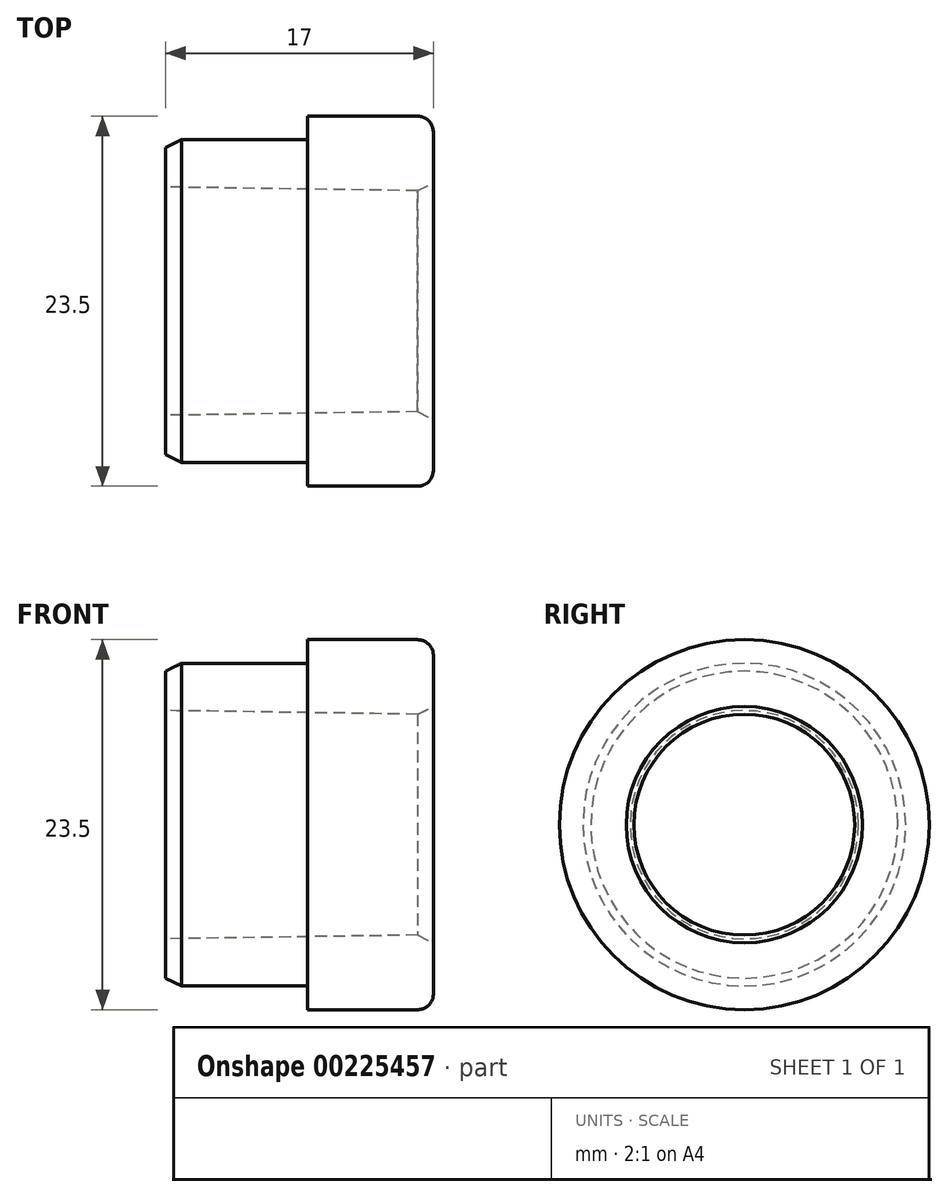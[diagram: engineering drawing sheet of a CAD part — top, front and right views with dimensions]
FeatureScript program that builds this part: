
annotation { "Feature Type Name" : "Feature", "Feature Type Description" : "" }
export const myFeature = defineFeature(function(context is Context, id is Id, definition is map)
    precondition{}
    {
        {
            var Q0;
            Q0=qCreatedBy(makeId("Top.planeOp"),FACE);
            var sketch = newSketch(context, id + "F0", { "sketchPlane" : qUnion([Q0])});
            skLineSegment(sketch, "E0", {"start": v(-17, 0) * mm, "end": v(0, 0) * mm, "construction": true});
            skLineSegment(sketch, "E1", {"start": v(0, 7) * mm, "end": v(0, 11.75) * mm});
            skLineSegment(sketch, "E2", {"start": v(0, 11.75) * mm, "end": v(-8, 11.75) * mm});
            skLineSegment(sketch, "E3", {"start": v(-8, 11.75) * mm, "end": v(-8, 10.25) * mm});
            skLineSegment(sketch, "E4", {"start": v(-8, 10.25) * mm, "end": v(-17, 10.25) * mm});
            skLineSegment(sketch, "E5", {"start": v(0, 7) * mm, "end": v(-17, 7.25) * mm});
            skLineSegment(sketch, "E6", {"start": v(-17, 7.25) * mm, "end": v(-17, 10.25) * mm});
            skLineSegment(sketch, "E7.MirrorCS", {"start": v(-17, -7.25) * mm, "end": v(-17, -10.25) * mm});
            skLineSegment(sketch, "E8.MirrorCS", {"start": v(0, -7) * mm, "end": v(0, -11.75) * mm});
            skLineSegment(sketch, "E9.MirrorCS", {"start": v(0, -11.75) * mm, "end": v(-8, -11.75) * mm});
            skLineSegment(sketch, "E10.MirrorCS", {"start": v(-8, -11.75) * mm, "end": v(-8, -10.25) * mm});
            skLineSegment(sketch, "E11.MirrorCS", {"start": v(-8, -10.25) * mm, "end": v(-17, -10.25) * mm});
            skLineSegment(sketch, "E12.MirrorCS", {"start": v(0, -7) * mm, "end": v(-17, -7.25) * mm});
            skSolve(sketch);
        }
        {
            var Q0;
            Q0=makeQuery(id+"F0.imprint","IMPRINT",FACE,{"disambiguationData":[TD([[makeQuery(id+"F0.imprint","IMPRINT",EDGE,{"derivedFrom":sQuery(id+"F0.wireOp",EDGE,"E7.MirrorCS")}),1.0]])]});
            var Q1;
            Q1=sQuery(id+"F0.wireOp",EDGE,"E0");
            revolve(context, id + "F1", {"entities" : qUnion([Q0]), "axis" : qUnion([Q1]), "revolveType" : RevolveType.FULL});
        }
        {
            var Q0;
            Q0=makeQuery(id+"F1.opRevolve","SWEPT_EDGE",EDGE,{"disambiguationData":[OSD([sQuery(id+"F0.wireOp",EDGE,"E7.MirrorCS"),sQuery(id+"F0.wireOp",EDGE,"E11.MirrorCS")])]});
            chamfer(context, id + "F2", {"entities" : qUnion([Q0]), "chamferType" : ChamferType.TWO_OFFSETS, "width1" : 0.5 * mm, "oppositeDirection" : false, "width2" : 1 * mm, "tangentPropagation" : true});
        }
        {
            var Q0;
            Q0=makeQuery(id+"F1.opRevolve","SWEPT_EDGE",EDGE,{"disambiguationData":[OSD([sQuery(id+"F0.wireOp",EDGE,"E8.MirrorCS"),sQuery(id+"F0.wireOp",EDGE,"E12.MirrorCS")])]});
            chamfer(context, id + "F3", {"entities" : qUnion([Q0]), "chamferType" : ChamferType.TWO_OFFSETS, "width1" : 1 * mm, "oppositeDirection" : true, "width2" : 0.5 * mm, "tangentPropagation" : true});
        }
        {
            var Q0;
            Q0=makeQuery(id+"F1.opRevolve","SWEPT_EDGE",EDGE,{"disambiguationData":[OSD([sQuery(id+"F0.wireOp",EDGE,"E8.MirrorCS"),sQuery(id+"F0.wireOp",EDGE,"E9.MirrorCS")])]});
            fillet(context, id + "F4", {"entities" : qUnion([Q0]), "radius" : 1 * mm, "tangentPropagation" : true, "allowEdgeOverflow" : false});
        }
    });
